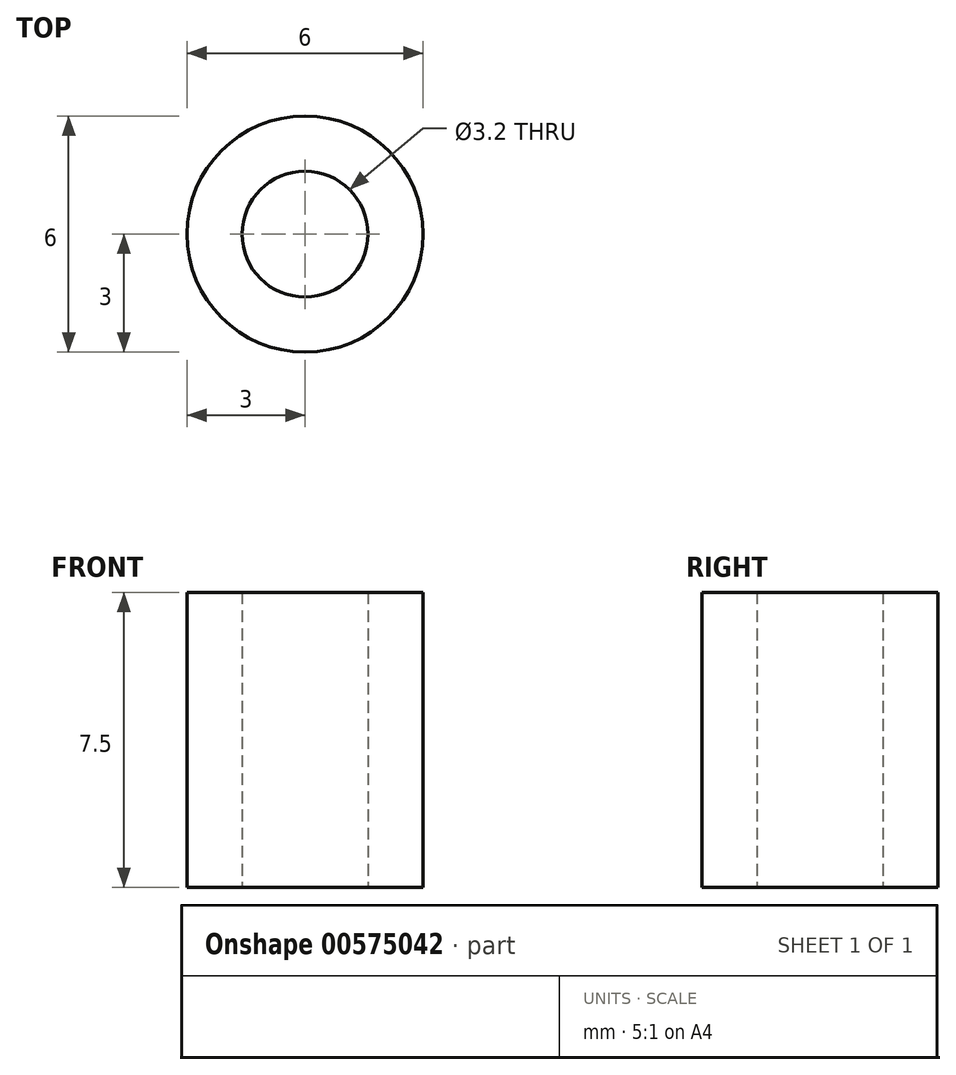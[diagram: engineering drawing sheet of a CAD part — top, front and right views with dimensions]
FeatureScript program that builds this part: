
annotation { "Feature Type Name" : "Feature", "Feature Type Description" : "" }
export const myFeature = defineFeature(function(context is Context, id is Id, definition is map)
    precondition{}
    {
        {
            var Q0;
            Q0=qCreatedBy(makeId("Top.planeOp"),FACE);
            var sketch = newSketch(context, id + "F0", { "sketchPlane" : qUnion([Q0])});
            skCircle(sketch, "E0", {"center": v(0, 0) * mm, "radius": 1.6 * mm});
            skCircle(sketch, "E1", {"center": v(0, 0) * mm, "radius": 3 * mm});
            skSolve(sketch);
        }
        {
            var Q0;
            Q0 = qSketchRegion(id + "F0", true);
            extrude(context, id + "F1", {"entities" : qUnion([Q0]), "depth" : 7.5 * mm, "offsetDistance" : 25 * mm});
        }
    });
